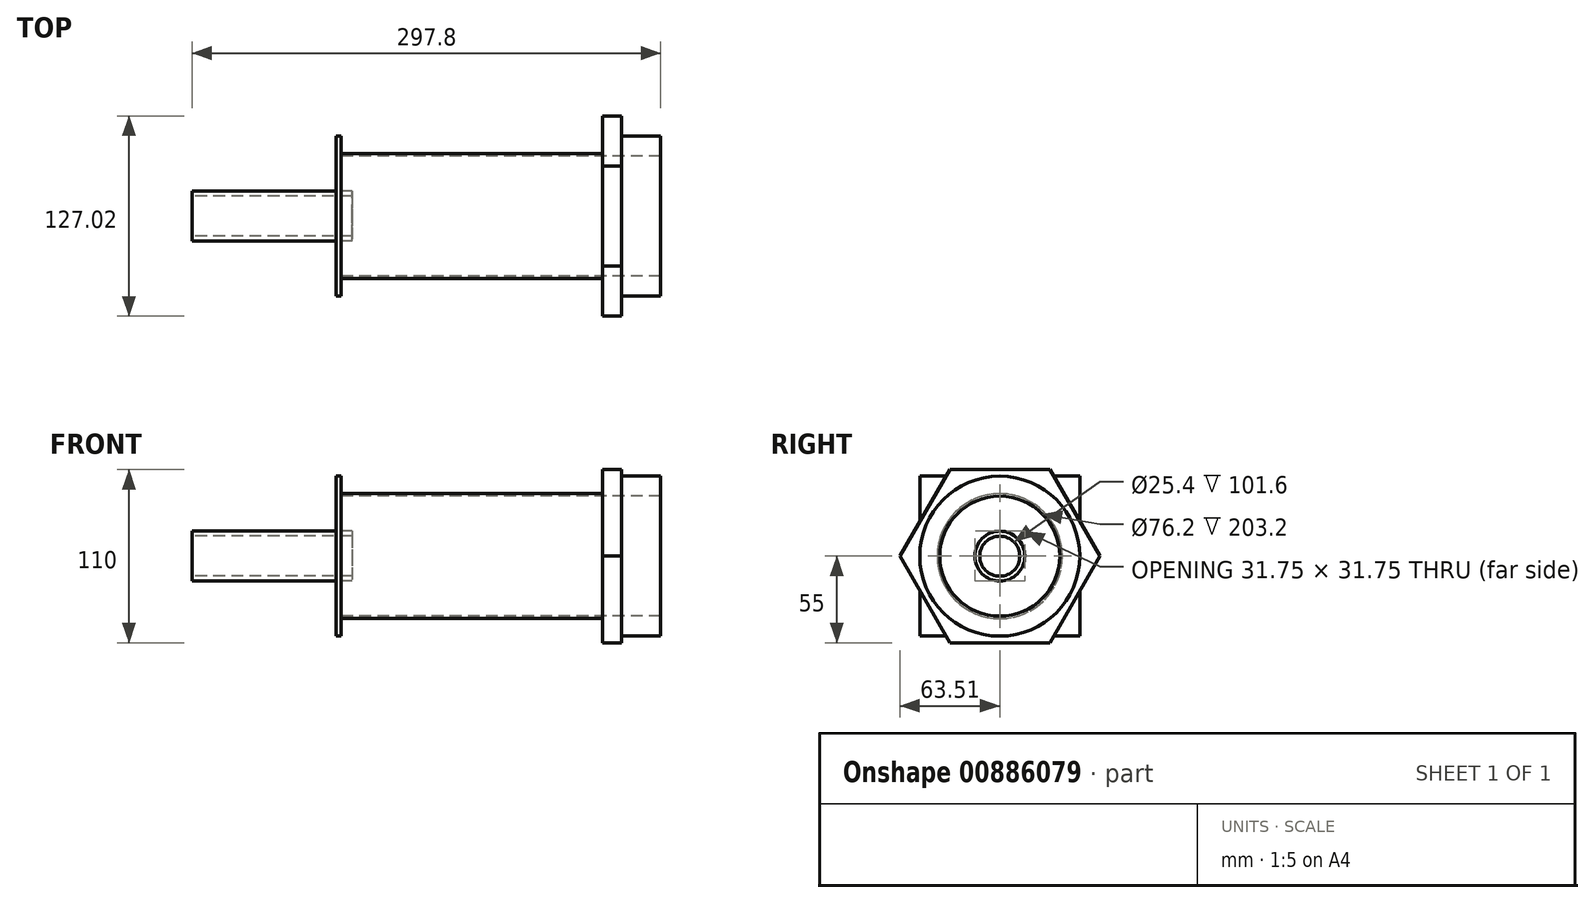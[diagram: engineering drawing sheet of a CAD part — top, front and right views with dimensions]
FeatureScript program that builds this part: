
annotation { "Feature Type Name" : "Feature", "Feature Type Description" : "" }
export const myFeature = defineFeature(function(context is Context, id is Id, definition is map)
    precondition{}
    {
        {
            var Q0;
            Q0=qCreatedBy(makeId("Front.planeOp"),FACE);
            var sketch = newSketch(context, id + "F0", { "sketchPlane" : qUnion([Q0])});
            skLineSegment(sketch, "E0", {"start": v(0, 0) * mm, "end": v(214.6, 0) * mm, "construction": true});
            skLineSegment(sketch, "E1", {"start": v(0, 15.88) * mm, "end": v(101.6, 15.88) * mm});
            skLineSegment(sketch, "E2", {"start": v(101.6, 15.88) * mm, "end": v(101.6, 12.7) * mm});
            skLineSegment(sketch, "E3", {"start": v(101.6, 12.7) * mm, "end": v(0, 12.7) * mm});
            skLineSegment(sketch, "E4", {"start": v(0, 15.88) * mm, "end": v(0, 12.7) * mm});
            skSolve(sketch);
        }
        {
            var Q0;
            Q0 = qSketchRegion(id + "F0", true);
            var Q1;
            Q1=sQuery(id+"F0.wireOp",EDGE,"E0");
            revolve(context, id + "F1", {"surfaceOperationType" : NewSurfaceOperationType.NEW, "entities" : qUnion([Q0]), "axis" : qUnion([Q1]), "revolveType" : RevolveType.FULL});
        }
        {
            var Q0;
            Q0=makeQuery(id+"F1.opRevolve","SWEPT_FACE",FACE,{"disambiguationData":[OSD([sQuery(id+"F0.wireOp",EDGE,"E2")])]});
            cPlane(context, id + "F2", {"entities" : qUnion([Q0]), "cplaneType" : CPlaneType.OFFSET, "offset" : 10 * mm, "oppositeDirection" : true, "width" : 150 * mm, "height" : 150 * mm});
        }
        {
            var Q0;
            Q0=qCreatedBy(id+"F2.planeOp",FACE);
            var sketch = newSketch(context, id + "F3", { "sketchPlane" : qUnion([Q0])});
            skCircle(sketch, "E5", {"center": v(0, 0) * mm, "radius": 14.29 * mm});
            skLineSegment(sketch, "E6.bottom", {"start": v(50.8, 50.8) * mm, "end": v(-50.8, 50.8) * mm});
            skLineSegment(sketch, "E6.top", {"start": v(50.8, -50.8) * mm, "end": v(-50.8, -50.8) * mm});
            skLineSegment(sketch, "E6.left", {"start": v(50.8, 50.8) * mm, "end": v(50.8, -50.8) * mm});
            skLineSegment(sketch, "E6.right", {"start": v(-50.8, 50.8) * mm, "end": v(-50.8, -50.8) * mm});
            skSolve(sketch);
        }
        {
            var Q0;
            Q0 = qSketchRegion(id + "F3", true);
            extrude(context, id + "F4", {"entities" : qUnion([Q0]), "operationType" : NewBodyOperationType.ADD, "depth" : 3 * mm, "offsetDistance" : 25 * mm});
        }
        {
            var Q0;
            Q0=makeQuery(id+"F4.opExtrude","CAP_FACE",FACE,{"disambiguationData":[OSD([sQuery(id+"F3.wireOp",EDGE,"E5"),sQuery(id+"F3.wireOp",EDGE,"E6.bottom"),sQuery(id+"F3.wireOp",EDGE,"E6.top"),sQuery(id+"F3.wireOp",EDGE,"E6.left"),sQuery(id+"F3.wireOp",EDGE,"E6.right")])],"isStart":false});
            var sketch = newSketch(context, id + "F5", { "sketchPlane" : qUnion([Q0])});
            skCircle(sketch, "E7", {"center": v(0, 0) * mm, "radius": 38.1 * mm});
            skCircle(sketch, "E8", {"center": v(0, 0) * mm, "radius": 39.69 * mm});
            skSolve(sketch);
        }
        {
            var Q0;
            Q0 = qSketchRegion(id + "F5", true);
            extrude(context, id + "F6", {"entities" : qUnion([Q0]), "operationType" : NewBodyOperationType.ADD, "depth" : 203.2 * mm, "offsetDistance" : 25 * mm});
        }
        {
            var Q0;
            Q0=makeQuery(id+"F6.opExtrude","CAP_FACE",FACE,{"disambiguationData":[OSD([sQuery(id+"F5.wireOp",EDGE,"E7"),sQuery(id+"F5.wireOp",EDGE,"E8")])],"isStart":false});
            var sketch = newSketch(context, id + "F7", { "sketchPlane" : qUnion([Q0])});
            skCircle(sketch, "E9", {"center": v(0, 0) * mm, "radius": 39.69 * mm});
            skCircle(sketch, "E10", {"center": v(0, 0) * mm, "radius": 50.8 * mm});
            skSolve(sketch);
        }
        {
            var Q0;
            Q0 = qSketchRegion(id + "F7", true);
            extrude(context, id + "F8", {"entities" : qUnion([Q0]), "operationType" : NewBodyOperationType.ADD, "oppositeDirection" : true, "depth" : 25 * mm, "offsetDistance" : 25 * mm});
        }
        {
            var Q0;
            Q0=makeQuery(id+"F8.opExtrude","CAP_FACE",FACE,{"disambiguationData":[OSD([sQuery(id+"F7.wireOp",EDGE,"E9"),sQuery(id+"F7.wireOp",EDGE,"E10")])],"isStart":false});
            var sketch = newSketch(context, id + "F9", { "sketchPlane" : qUnion([Q0])});
            skCircle(sketch, "E11", {"center": v(0, 0) * mm, "radius": 39.67 * mm});
            skLineSegment(sketch, "E12", {"start": v(31.75, 55) * mm, "end": v(-31.75, 55) * mm});
            skLineSegment(sketch, "E13", {"start": v(-31.75, 55) * mm, "end": v(-63.5, 0) * mm});
            skLineSegment(sketch, "E14", {"start": v(-63.5, 0) * mm, "end": v(-31.75, -55) * mm});
            skLineSegment(sketch, "E15", {"start": v(-31.75, -55) * mm, "end": v(31.75, -55) * mm});
            skLineSegment(sketch, "E16", {"start": v(31.75, -55) * mm, "end": v(63.5, 0) * mm});
            skLineSegment(sketch, "E17", {"start": v(63.5, 0) * mm, "end": v(31.75, 55) * mm});
            skLineSegment(sketch, "E18", {"start": v(0, 0) * mm, "end": v(31.75, 55) * mm, "construction": true});
            skLineSegment(sketch, "E19", {"start": v(0, 0) * mm, "end": v(-31.75, -55) * mm, "construction": true});
            skLineSegment(sketch, "E20", {"start": v(0, 0) * mm, "end": v(-31.75, 55) * mm, "construction": true});
            skLineSegment(sketch, "E21", {"start": v(0, 0) * mm, "end": v(-63.5, 0) * mm, "construction": true});
            skLineSegment(sketch, "E22", {"start": v(0, 0) * mm, "end": v(31.75, -55) * mm, "construction": true});
            skLineSegment(sketch, "E23", {"start": v(0, 0) * mm, "end": v(63.5, 0) * mm, "construction": true});
            skCircle(sketch, "E24", {"center": v(0, 0) * mm, "radius": 55 * mm, "construction": true});
            skSolve(sketch);
        }
        {
            var Q0;
            Q0 = qSketchRegion(id + "F9", true);
            extrude(context, id + "F10", {"entities" : qUnion([Q0]), "operationType" : NewBodyOperationType.ADD, "depth" : 12 * mm, "offsetDistance" : 25 * mm});
        }
    });
